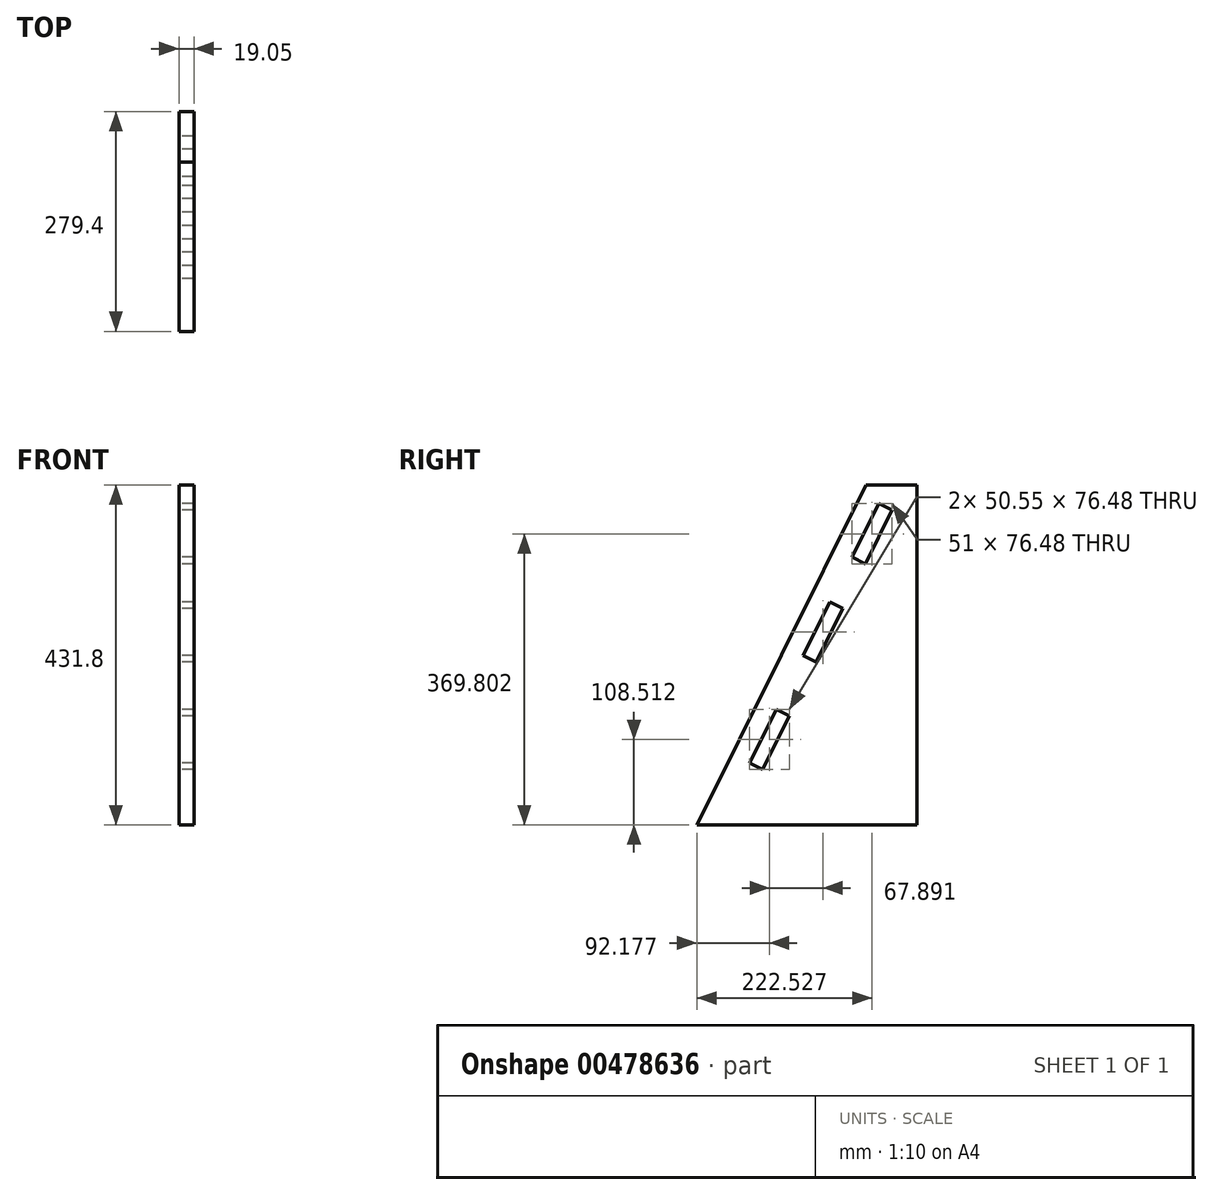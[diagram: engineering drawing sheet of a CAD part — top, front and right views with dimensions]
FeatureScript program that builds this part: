
annotation { "Feature Type Name" : "Feature", "Feature Type Description" : "" }
export const myFeature = defineFeature(function(context is Context, id is Id, definition is map)
    precondition{}
    {
        {
            var Q0;
            Q0=qCreatedBy(makeId("Right.planeOp"),FACE);
            var sketch = newSketch(context, id + "F0", { "sketchPlane" : qUnion([Q0])});
            skLineSegment(sketch, "E0", {"start": v(-185.34, -228.02) * mm, "end": v(29.51, 203.78) * mm});
            skLineSegment(sketch, "E1", {"start": v(94.06, 203.78) * mm, "end": v(94.06, -228.02) * mm});
            skLineSegment(sketch, "E2", {"start": v(94.06, -228.02) * mm, "end": v(-185.34, -228.02) * mm});
            skLineSegment(sketch, "E3", {"start": v(29.51, 203.78) * mm, "end": v(94.06, 203.78) * mm});
            skLineSegment(sketch, "E4", {"start": v(-50.55, -13.05) * mm, "end": v(-16.6, 55.18) * mm});
            skLineSegment(sketch, "E5", {"start": v(-16.6, 55.18) * mm, "end": v(0, 46.92) * mm});
            skLineSegment(sketch, "E6", {"start": v(0, 46.92) * mm, "end": v(-33.95, -21.3) * mm});
            skLineSegment(sketch, "E7", {"start": v(-33.95, -21.3) * mm, "end": v(-50.55, -13.05) * mm});
            skLineSegment(sketch, "E8.MirrorCS", {"start": v(11.69, 112.03) * mm, "end": v(28.74, 103.54) * mm});
            skLineSegment(sketch, "E9.MirrorCS", {"start": v(45.63, 180.25) * mm, "end": v(11.69, 112.03) * mm});
            skLineSegment(sketch, "E10.MirrorCS", {"start": v(28.74, 103.54) * mm, "end": v(62.69, 171.76) * mm});
            skLineSegment(sketch, "E11.MirrorCS", {"start": v(62.69, 171.76) * mm, "end": v(46.09, 180.02) * mm});
            skLineSegment(sketch, "E12.MirrorCS", {"start": v(-67.9, -89.53) * mm, "end": v(-84.5, -81.27) * mm});
            skLineSegment(sketch, "E13.MirrorCS", {"start": v(-84.5, -81.27) * mm, "end": v(-118.44, -149.49) * mm});
            skLineSegment(sketch, "E14.MirrorCS", {"start": v(-118.44, -149.49) * mm, "end": v(-101.38, -157.97) * mm});
            skLineSegment(sketch, "E15.MirrorCS", {"start": v(-101.84, -157.75) * mm, "end": v(-67.9, -89.53) * mm});
            skLineSegment(sketch, "E16.bottom", {"start": v(-83.74, -228.02) * mm, "end": v(17.86, -228.02) * mm});
            skLineSegment(sketch, "E16.top", {"start": v(-83.74, -246.56) * mm, "end": v(17.86, -246.56) * mm});
            skLineSegment(sketch, "E16.left", {"start": v(-83.74, -228.02) * mm, "end": v(-83.74, -246.56) * mm});
            skLineSegment(sketch, "E16.right", {"start": v(17.86, -228.02) * mm, "end": v(17.86, -246.56) * mm});
            skLineSegment(sketch, "E17", {"start": v(46.09, 180.02) * mm, "end": v(11.69, 112.03) * mm});
            skSolve(sketch);
        }
        {
            var Q0;
            Q0=makeQuery(id+"F0.imprint","IMPRINT",FACE,{"disambiguationData":[TD([[makeQuery(id+"F0.imprint","IMPRINT",EDGE,{"derivedFrom":sQuery(id+"F0.wireOp",EDGE,"E16.bottom")}),-1.0]])]});
            var Q1;
            {var subQ0=sQuery(id+"F0.wireOp",EDGE,"E0");Q1=makeQuery(id+"F0.imprint","IMPRINT",FACE,{"disambiguationData":[TD([[makeQuery(id+"F0.imprint","IMPRINT",EDGE,{"derivedFrom":subQ0}),-1.0]])]});}
            extrude(context, id + "F1", {"entities" : qUnion([Q0, Q1]), "depth" : 19.05 * mm, "offsetDistance" : 25.4 * mm});
        }
    });
